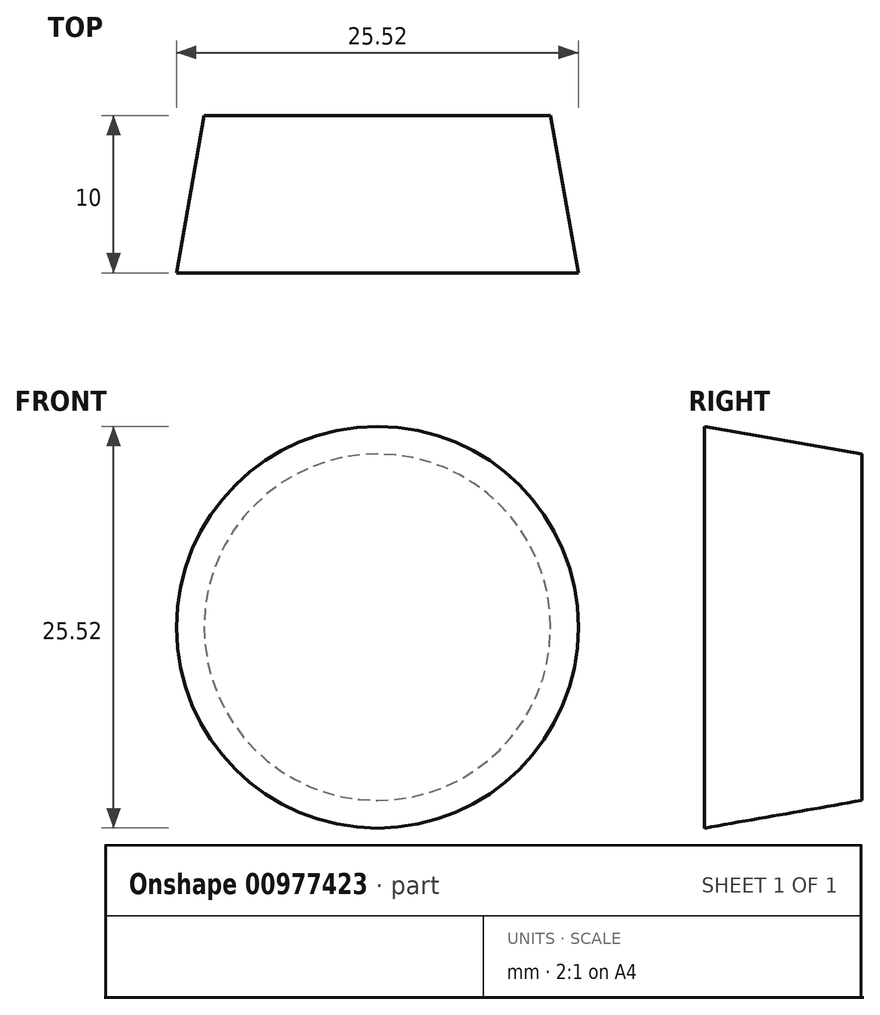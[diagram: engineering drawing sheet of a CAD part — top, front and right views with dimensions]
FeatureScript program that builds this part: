
annotation { "Feature Type Name" : "Feature", "Feature Type Description" : "" }
export const myFeature = defineFeature(function(context is Context, id is Id, definition is map)
    precondition{}
    {
        {
            var Q0;
            Q0=qCreatedBy(makeId("Front.planeOp"),FACE);
            var sketch = newSketch(context, id + "F0", { "sketchPlane" : qUnion([Q0])});
            skCircle(sketch, "E0", {"center": v(0, 0) * mm, "radius": 11 * mm});
            skSolve(sketch);
        }
        {
            var Q0;
            Q0=qSketchRegion(id+"F0",true);
            extrude(context, id + "F1", {"entities" : qUnion([Q0]), "depth" : 10 * mm, "offsetDistance" : 25 * mm, "hasDraft" : true, "draftAngle" : 10 * degree});
        }
        {
            var Q0;
            Q0=makeQuery(id+"F1.opExtrude","CAP_FACE",FACE,{"disambiguationData":[OSD([sQuery(id+"F0.wireOp",EDGE,"E0")])],"isStart":false});
            var sketch = newSketch(context, id + "F2", { "sketchPlane" : qUnion([Q0])});
            skLineSegment(sketch, "E1", {"start": v(0, 15) * mm, "end": v(0, -15) * mm, "construction": true});
            skArc(sketch, "E2", {"start": v(0, -15) * mm, "mid": v(15, 0) * mm, "end": v(0, 15) * mm});
            skSolve(sketch);
        }
        {
            var Q0;
            Q0=qSketchRegion(id+"F2",true);
            var Q1;
            Q1=sQuery(id+"F2.wireOp",EDGE,"E2");
            var Q2;
            Q2=sQuery(id+"F2.wireOp",EDGE,"E1");
            revolve(context, id + "F3", {"bodyType" : ToolBodyType.SURFACE, "surfaceOperationType" : NewSurfaceOperationType.NEW, "entities" : qUnion([Q0]), "surfaceEntities" : qUnion([Q1]), "axis" : qUnion([Q2]), "revolveType" : RevolveType.ONE_DIRECTION, "angle" : 180 * degree});
        }
    });
